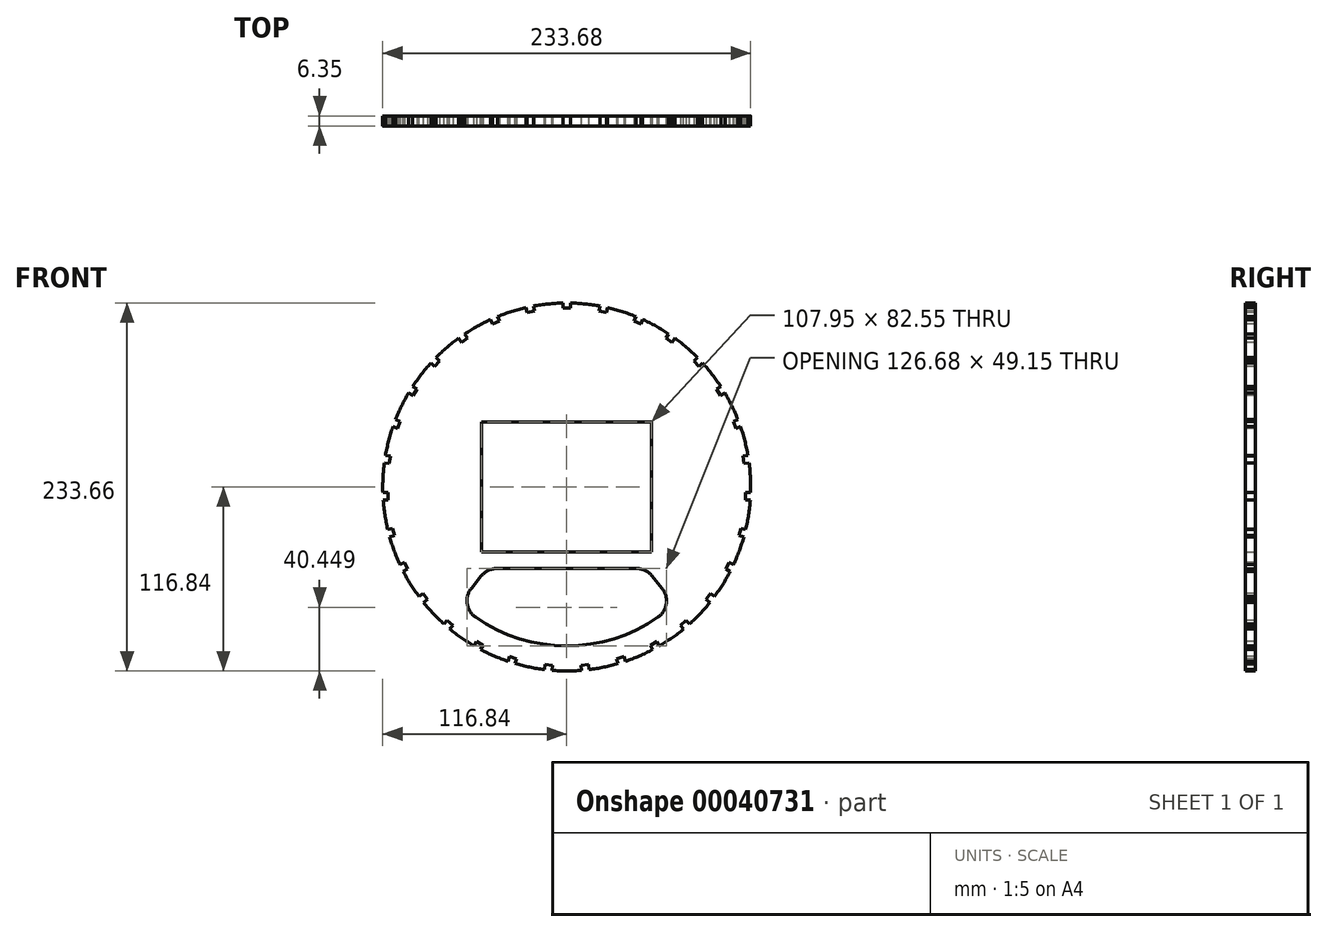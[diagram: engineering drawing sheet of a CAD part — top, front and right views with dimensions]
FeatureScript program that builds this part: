
annotation { "Feature Type Name" : "Feature", "Feature Type Description" : "" }
export const myFeature = defineFeature(function(context is Context, id is Id, definition is map)
    precondition{}
    {
        {
            var Q0;
            Q0=qCreatedBy(makeId("Front.planeOp"),FACE);
            var sketch = newSketch(context, id + "F0", { "sketchPlane" : qUnion([Q0])});
            skCircle(sketch, "E0", {"center": v(0, 0) * mm, "radius": 116.84 * mm});
            skLineSegment(sketch, "E1.bottom", {"start": v(-53.97, 41.28) * mm, "end": v(53.98, 41.28) * mm});
            skLineSegment(sketch, "E1.top", {"start": v(-53.97, -41.27) * mm, "end": v(53.98, -41.27) * mm});
            skLineSegment(sketch, "E1.left", {"start": v(-53.97, 41.28) * mm, "end": v(-53.97, -41.27) * mm});
            skLineSegment(sketch, "E1.right", {"start": v(53.98, 41.28) * mm, "end": v(53.98, -41.27) * mm});
            skLineSegment(sketch, "E2", {"start": v(0, 121.96) * mm, "end": v(0, -123.35) * mm, "construction": true});
            skLineSegment(sketch, "E3", {"start": v(-144.98, 0) * mm, "end": v(150.29, 0) * mm, "construction": true});
            skArc(sketch, "E4", {"start": v(-57.96, -82.67) * mm, "mid": v(0, -100.97) * mm, "end": v(57.96, -82.67) * mm});
            skLineSegment(sketch, "E5", {"start": v(-60.54, -64.28) * mm, "end": v(-54.26, -56.53) * mm});
            skLineSegment(sketch, "E6", {"start": v(-44.38, -51.82) * mm, "end": v(44.38, -51.82) * mm});
            skLineSegment(sketch, "E7", {"start": v(54.26, -56.53) * mm, "end": v(60.54, -64.28) * mm});
            skPoint(sketch, "E8.visualSharp", {"position": v(-50.44, -51.82) * mm});
            skArc(sketch, "E8.filletArc", {"start": v(-44.38, -51.82) * mm, "mid": v(-49.85, -53.05) * mm, "end": v(-54.26, -56.53) * mm});
            skPoint(sketch, "E9.visualSharp", {"position": v(50.44, -51.82) * mm});
            skArc(sketch, "E9.filletArc", {"start": v(54.26, -56.53) * mm, "mid": v(49.85, -53.05) * mm, "end": v(44.38, -51.82) * mm});
            skPoint(sketch, "E10.visualSharp", {"position": v(-68.52, -74.15) * mm});
            skArc(sketch, "E10.filletArc", {"start": v(-60.54, -64.28) * mm, "mid": v(-63.24, -74.04) * mm, "end": v(-57.96, -82.67) * mm});
            skPoint(sketch, "E11.visualSharp", {"position": v(68.52, -74.15) * mm});
            skArc(sketch, "E11.filletArc", {"start": v(57.96, -82.67) * mm, "mid": v(63.24, -74.04) * mm, "end": v(60.54, -64.28) * mm});
            skLineSegment(sketch, "E12.anchor1", {"start": v(0, 0) * mm, "end": v(-68.52, -74.15) * mm, "construction": true});
            skLineSegment(sketch, "E12.anchor2", {"start": v(0, 0) * mm, "end": v(-68.52, -74.15) * mm, "construction": true});
            skSolve(sketch);
        }
        {
            var Q0;
            Q0=makeQuery(id+"F0.imprint","IMPRINT",FACE,{"disambiguationData":[TD([[makeQuery(id+"F0.imprint","IMPRINT",EDGE,{"derivedFrom":sQuery(id+"F0.wireOp",EDGE,"E0")}),1.0]])]});
            extrude(context, id + "F1", {"entities" : qUnion([Q0]), "depth" : 6.35 * mm});
        }
        {
            var Q0;
            Q0=makeQuery(id+"F1.opExtrude","CAP_FACE",FACE,{"disambiguationData":[OSD([sQuery(id+"F0.wireOp",EDGE,"E0"),sQuery(id+"F0.wireOp",EDGE,"E1.bottom"),sQuery(id+"F0.wireOp",EDGE,"E1.top"),sQuery(id+"F0.wireOp",EDGE,"E1.left"),sQuery(id+"F0.wireOp",EDGE,"E1.right"),sQuery(id+"F0.wireOp",EDGE,"E4"),sQuery(id+"F0.wireOp",EDGE,"E5"),sQuery(id+"F0.wireOp",EDGE,"E6"),sQuery(id+"F0.wireOp",EDGE,"E7"),sQuery(id+"F0.wireOp",EDGE,"E8.filletArc"),sQuery(id+"F0.wireOp",EDGE,"E9.filletArc"),sQuery(id+"F0.wireOp",EDGE,"E10.filletArc"),sQuery(id+"F0.wireOp",EDGE,"E11.filletArc")])],"isStart":false});
            var sketch = newSketch(context, id + "F2", { "sketchPlane" : qUnion([Q0])});
            skLineSegment(sketch, "E13", {"start": v(0, 66.33) * mm, "end": v(0, 127.65) * mm, "construction": true});
            skLineSegment(sketch, "E14.bottom", {"start": v(-2.38, 116.84) * mm, "end": v(2.38, 116.84) * mm});
            skLineSegment(sketch, "E14.top", {"start": v(-2.38, 113.66) * mm, "end": v(2.38, 113.66) * mm});
            skLineSegment(sketch, "E14.left", {"start": v(-2.38, 116.84) * mm, "end": v(-2.38, 113.66) * mm});
            skLineSegment(sketch, "E14.right", {"start": v(2.38, 116.84) * mm, "end": v(2.38, 113.66) * mm});
            skLineSegment(sketch, "E15.1.0", {"start": v(21.19, 114.93) * mm, "end": v(25.85, 113.97) * mm});
            skLineSegment(sketch, "E15.1.1", {"start": v(20.55, 111.82) * mm, "end": v(25.21, 110.86) * mm});
            skLineSegment(sketch, "E15.1.2", {"start": v(21.19, 114.93) * mm, "end": v(20.55, 111.82) * mm});
            skLineSegment(sketch, "E15.1.3", {"start": v(25.85, 113.97) * mm, "end": v(25.21, 110.86) * mm});
            skLineSegment(sketch, "E15.2.0", {"start": v(43.89, 108.31) * mm, "end": v(48.26, 106.43) * mm});
            skLineSegment(sketch, "E15.2.1", {"start": v(42.64, 105.4) * mm, "end": v(47.01, 103.51) * mm});
            skLineSegment(sketch, "E15.2.2", {"start": v(43.89, 108.31) * mm, "end": v(42.64, 105.4) * mm});
            skLineSegment(sketch, "E15.2.3", {"start": v(48.26, 106.43) * mm, "end": v(47.01, 103.51) * mm});
            skLineSegment(sketch, "E15.3.0", {"start": v(64.8, 97.26) * mm, "end": v(68.7, 94.54) * mm});
            skLineSegment(sketch, "E15.3.1", {"start": v(62.98, 94.65) * mm, "end": v(66.89, 91.93) * mm});
            skLineSegment(sketch, "E15.3.2", {"start": v(64.8, 97.26) * mm, "end": v(62.98, 94.65) * mm});
            skLineSegment(sketch, "E15.3.3", {"start": v(68.7, 94.54) * mm, "end": v(66.89, 91.93) * mm});
            skLineSegment(sketch, "E15.4.0", {"start": v(83.04, 82.22) * mm, "end": v(86.33, 78.77) * mm});
            skLineSegment(sketch, "E15.4.1", {"start": v(80.74, 80.04) * mm, "end": v(84.02, 76.59) * mm});
            skLineSegment(sketch, "E15.4.2", {"start": v(83.04, 82.22) * mm, "end": v(80.74, 80.04) * mm});
            skLineSegment(sketch, "E15.4.3", {"start": v(86.33, 78.77) * mm, "end": v(84.02, 76.59) * mm});
            skLineSegment(sketch, "E15.5.0", {"start": v(97.9, 63.83) * mm, "end": v(100.42, 59.78) * mm});
            skLineSegment(sketch, "E15.5.1", {"start": v(95.2, 62.15) * mm, "end": v(97.72, 58.1) * mm});
            skLineSegment(sketch, "E15.5.2", {"start": v(97.9, 63.83) * mm, "end": v(95.2, 62.15) * mm});
            skLineSegment(sketch, "E15.5.3", {"start": v(100.42, 59.78) * mm, "end": v(97.72, 58.1) * mm});
            skLineSegment(sketch, "E15.6.0", {"start": v(108.74, 42.81) * mm, "end": v(110.4, 38.35) * mm});
            skLineSegment(sketch, "E15.6.1", {"start": v(105.76, 41.7) * mm, "end": v(107.42, 37.24) * mm});
            skLineSegment(sketch, "E15.6.2", {"start": v(108.74, 42.81) * mm, "end": v(105.76, 41.7) * mm});
            skLineSegment(sketch, "E15.6.3", {"start": v(110.4, 38.35) * mm, "end": v(107.42, 37.24) * mm});
            skLineSegment(sketch, "E15.7.0", {"start": v(115.13, 20.05) * mm, "end": v(115.85, 15.34) * mm});
            skLineSegment(sketch, "E15.7.1", {"start": v(112, 19.57) * mm, "end": v(112.71, 14.86) * mm});
            skLineSegment(sketch, "E15.7.2", {"start": v(115.13, 20.05) * mm, "end": v(112, 19.57) * mm});
            skLineSegment(sketch, "E15.7.3", {"start": v(115.85, 15.34) * mm, "end": v(112.71, 14.86) * mm});
            skLineSegment(sketch, "E15.8.0", {"start": v(116.81, -3.54) * mm, "end": v(116.57, -8.3) * mm});
            skLineSegment(sketch, "E15.8.1", {"start": v(113.64, -3.38) * mm, "end": v(113.4, -8.13) * mm});
            skLineSegment(sketch, "E15.8.2", {"start": v(116.81, -3.54) * mm, "end": v(113.64, -3.38) * mm});
            skLineSegment(sketch, "E15.8.3", {"start": v(116.57, -8.3) * mm, "end": v(113.4, -8.13) * mm});
            skLineSegment(sketch, "E15.9.0", {"start": v(113.7, -26.98) * mm, "end": v(112.51, -31.6) * mm});
            skLineSegment(sketch, "E15.9.1", {"start": v(110.63, -26.18) * mm, "end": v(109.44, -30.8) * mm});
            skLineSegment(sketch, "E15.9.2", {"start": v(113.7, -26.98) * mm, "end": v(110.63, -26.18) * mm});
            skLineSegment(sketch, "E15.9.3", {"start": v(112.51, -31.6) * mm, "end": v(109.44, -30.8) * mm});
            skLineSegment(sketch, "E15.10.0", {"start": v(105.95, -49.32) * mm, "end": v(103.85, -53.6) * mm});
            skLineSegment(sketch, "E15.10.1", {"start": v(103.1, -47.92) * mm, "end": v(101, -52.2) * mm});
            skLineSegment(sketch, "E15.10.2", {"start": v(105.95, -49.32) * mm, "end": v(103.1, -47.92) * mm});
            skLineSegment(sketch, "E15.10.3", {"start": v(103.85, -53.6) * mm, "end": v(101, -52.2) * mm});
            skLineSegment(sketch, "E15.11.0", {"start": v(93.85, -69.63) * mm, "end": v(90.94, -73.4) * mm});
            skLineSegment(sketch, "E15.11.1", {"start": v(91.34, -67.7) * mm, "end": v(88.43, -71.46) * mm});
            skLineSegment(sketch, "E15.11.2", {"start": v(93.85, -69.63) * mm, "end": v(91.34, -67.7) * mm});
            skLineSegment(sketch, "E15.11.3", {"start": v(90.94, -73.4) * mm, "end": v(88.43, -71.46) * mm});
            skLineSegment(sketch, "E15.12.0", {"start": v(77.91, -87.1) * mm, "end": v(74.3, -90.2) * mm});
            skLineSegment(sketch, "E15.12.1", {"start": v(75.85, -84.7) * mm, "end": v(72.23, -87.8) * mm});
            skLineSegment(sketch, "E15.12.2", {"start": v(77.91, -87.1) * mm, "end": v(75.85, -84.7) * mm});
            skLineSegment(sketch, "E15.12.3", {"start": v(74.3, -90.2) * mm, "end": v(72.23, -87.8) * mm});
            skLineSegment(sketch, "E15.13.0", {"start": v(58.79, -101) * mm, "end": v(54.62, -103.31) * mm});
            skLineSegment(sketch, "E15.13.1", {"start": v(57.24, -98.23) * mm, "end": v(53.08, -100.54) * mm});
            skLineSegment(sketch, "E15.13.2", {"start": v(58.79, -101) * mm, "end": v(57.24, -98.23) * mm});
            skLineSegment(sketch, "E15.13.3", {"start": v(54.62, -103.31) * mm, "end": v(53.08, -100.54) * mm});
            skLineSegment(sketch, "E15.14.0", {"start": v(37.25, -110.77) * mm, "end": v(32.7, -112.2) * mm});
            skLineSegment(sketch, "E15.14.1", {"start": v(36.3, -107.74) * mm, "end": v(31.76, -109.16) * mm});
            skLineSegment(sketch, "E15.14.2", {"start": v(37.25, -110.77) * mm, "end": v(36.3, -107.74) * mm});
            skLineSegment(sketch, "E15.14.3", {"start": v(32.7, -112.2) * mm, "end": v(31.76, -109.16) * mm});
            skLineSegment(sketch, "E15.15.0", {"start": v(14.2, -116) * mm, "end": v(9.45, -116.48) * mm});
            skLineSegment(sketch, "E15.15.1", {"start": v(13.87, -112.84) * mm, "end": v(9.13, -113.32) * mm});
            skLineSegment(sketch, "E15.15.2", {"start": v(14.2, -116) * mm, "end": v(13.87, -112.84) * mm});
            skLineSegment(sketch, "E15.15.3", {"start": v(9.45, -116.48) * mm, "end": v(9.13, -113.32) * mm});
            skLineSegment(sketch, "E15.16.0", {"start": v(-9.45, -116.48) * mm, "end": v(-14.19, -116) * mm});
            skLineSegment(sketch, "E15.16.1", {"start": v(-9.13, -113.32) * mm, "end": v(-13.87, -112.84) * mm});
            skLineSegment(sketch, "E15.16.2", {"start": v(-9.45, -116.48) * mm, "end": v(-9.13, -113.32) * mm});
            skLineSegment(sketch, "E15.16.3", {"start": v(-14.19, -116) * mm, "end": v(-13.87, -112.84) * mm});
            skLineSegment(sketch, "E15.17.0", {"start": v(-32.7, -112.2) * mm, "end": v(-37.25, -110.77) * mm});
            skLineSegment(sketch, "E15.17.1", {"start": v(-31.75, -109.17) * mm, "end": v(-36.3, -107.74) * mm});
            skLineSegment(sketch, "E15.17.2", {"start": v(-32.7, -112.2) * mm, "end": v(-31.75, -109.17) * mm});
            skLineSegment(sketch, "E15.17.3", {"start": v(-37.25, -110.77) * mm, "end": v(-36.3, -107.74) * mm});
            skLineSegment(sketch, "E15.18.0", {"start": v(-54.62, -103.31) * mm, "end": v(-58.78, -101) * mm});
            skLineSegment(sketch, "E15.18.1", {"start": v(-53.08, -100.54) * mm, "end": v(-57.24, -98.23) * mm});
            skLineSegment(sketch, "E15.18.2", {"start": v(-54.62, -103.31) * mm, "end": v(-53.08, -100.54) * mm});
            skLineSegment(sketch, "E15.18.3", {"start": v(-58.78, -101) * mm, "end": v(-57.24, -98.23) * mm});
            skLineSegment(sketch, "E15.19.0", {"start": v(-74.3, -90.2) * mm, "end": v(-77.91, -87.1) * mm});
            skLineSegment(sketch, "E15.19.1", {"start": v(-72.23, -87.8) * mm, "end": v(-75.84, -84.7) * mm});
            skLineSegment(sketch, "E15.19.2", {"start": v(-74.3, -90.2) * mm, "end": v(-72.23, -87.8) * mm});
            skLineSegment(sketch, "E15.19.3", {"start": v(-77.91, -87.1) * mm, "end": v(-75.84, -84.7) * mm});
            skLineSegment(sketch, "E15.20.0", {"start": v(-90.94, -73.4) * mm, "end": v(-93.85, -69.64) * mm});
            skLineSegment(sketch, "E15.20.1", {"start": v(-88.43, -71.46) * mm, "end": v(-91.34, -67.7) * mm});
            skLineSegment(sketch, "E15.20.2", {"start": v(-90.94, -73.4) * mm, "end": v(-88.43, -71.46) * mm});
            skLineSegment(sketch, "E15.20.3", {"start": v(-93.85, -69.64) * mm, "end": v(-91.34, -67.7) * mm});
            skLineSegment(sketch, "E15.21.0", {"start": v(-103.85, -53.6) * mm, "end": v(-105.95, -49.32) * mm});
            skLineSegment(sketch, "E15.21.1", {"start": v(-101, -52.2) * mm, "end": v(-103.1, -47.92) * mm});
            skLineSegment(sketch, "E15.21.2", {"start": v(-103.85, -53.6) * mm, "end": v(-101, -52.2) * mm});
            skLineSegment(sketch, "E15.21.3", {"start": v(-105.95, -49.32) * mm, "end": v(-103.1, -47.92) * mm});
            skLineSegment(sketch, "E15.22.0", {"start": v(-112.51, -31.6) * mm, "end": v(-113.7, -26.98) * mm});
            skLineSegment(sketch, "E15.22.1", {"start": v(-109.44, -30.8) * mm, "end": v(-110.63, -26.19) * mm});
            skLineSegment(sketch, "E15.22.2", {"start": v(-112.51, -31.6) * mm, "end": v(-109.44, -30.8) * mm});
            skLineSegment(sketch, "E15.22.3", {"start": v(-113.7, -26.98) * mm, "end": v(-110.63, -26.19) * mm});
            skLineSegment(sketch, "E15.23.0", {"start": v(-116.57, -8.3) * mm, "end": v(-116.81, -3.54) * mm});
            skLineSegment(sketch, "E15.23.1", {"start": v(-113.4, -8.14) * mm, "end": v(-113.64, -3.38) * mm});
            skLineSegment(sketch, "E15.23.2", {"start": v(-116.57, -8.3) * mm, "end": v(-113.4, -8.14) * mm});
            skLineSegment(sketch, "E15.23.3", {"start": v(-116.81, -3.54) * mm, "end": v(-113.64, -3.38) * mm});
            skLineSegment(sketch, "E15.24.0", {"start": v(-115.85, 15.34) * mm, "end": v(-115.13, 20.05) * mm});
            skLineSegment(sketch, "E15.24.1", {"start": v(-112.72, 14.86) * mm, "end": v(-112, 19.56) * mm});
            skLineSegment(sketch, "E15.24.2", {"start": v(-115.85, 15.34) * mm, "end": v(-112.72, 14.86) * mm});
            skLineSegment(sketch, "E15.24.3", {"start": v(-115.13, 20.05) * mm, "end": v(-112, 19.56) * mm});
            skLineSegment(sketch, "E15.25.0", {"start": v(-110.4, 38.34) * mm, "end": v(-108.74, 42.81) * mm});
            skLineSegment(sketch, "E15.25.1", {"start": v(-107.42, 37.24) * mm, "end": v(-105.76, 41.7) * mm});
            skLineSegment(sketch, "E15.25.2", {"start": v(-110.4, 38.34) * mm, "end": v(-107.42, 37.24) * mm});
            skLineSegment(sketch, "E15.25.3", {"start": v(-108.74, 42.81) * mm, "end": v(-105.76, 41.7) * mm});
            skLineSegment(sketch, "E15.26.0", {"start": v(-100.42, 59.78) * mm, "end": v(-97.9, 63.82) * mm});
            skLineSegment(sketch, "E15.26.1", {"start": v(-97.72, 58.1) * mm, "end": v(-95.2, 62.14) * mm});
            skLineSegment(sketch, "E15.26.2", {"start": v(-100.42, 59.78) * mm, "end": v(-97.72, 58.1) * mm});
            skLineSegment(sketch, "E15.26.3", {"start": v(-97.9, 63.82) * mm, "end": v(-95.2, 62.14) * mm});
            skLineSegment(sketch, "E15.27.0", {"start": v(-86.33, 78.77) * mm, "end": v(-83.05, 82.22) * mm});
            skLineSegment(sketch, "E15.27.1", {"start": v(-84.03, 76.58) * mm, "end": v(-80.74, 80.04) * mm});
            skLineSegment(sketch, "E15.27.2", {"start": v(-86.33, 78.77) * mm, "end": v(-84.03, 76.58) * mm});
            skLineSegment(sketch, "E15.27.3", {"start": v(-83.05, 82.22) * mm, "end": v(-80.74, 80.04) * mm});
            skLineSegment(sketch, "E15.28.0", {"start": v(-68.7, 94.54) * mm, "end": v(-64.8, 97.26) * mm});
            skLineSegment(sketch, "E15.28.1", {"start": v(-66.89, 91.93) * mm, "end": v(-62.98, 94.65) * mm});
            skLineSegment(sketch, "E15.28.2", {"start": v(-68.7, 94.54) * mm, "end": v(-66.89, 91.93) * mm});
            skLineSegment(sketch, "E15.28.3", {"start": v(-64.8, 97.26) * mm, "end": v(-62.98, 94.65) * mm});
            skLineSegment(sketch, "E15.29.0", {"start": v(-48.27, 106.43) * mm, "end": v(-43.9, 108.3) * mm});
            skLineSegment(sketch, "E15.29.1", {"start": v(-47.01, 103.51) * mm, "end": v(-42.64, 105.4) * mm});
            skLineSegment(sketch, "E15.29.2", {"start": v(-48.27, 106.43) * mm, "end": v(-47.01, 103.51) * mm});
            skLineSegment(sketch, "E15.29.3", {"start": v(-43.9, 108.3) * mm, "end": v(-42.64, 105.4) * mm});
            skLineSegment(sketch, "E15.30.0", {"start": v(-25.85, 113.97) * mm, "end": v(-21.19, 114.93) * mm});
            skLineSegment(sketch, "E15.30.1", {"start": v(-25.21, 110.86) * mm, "end": v(-20.55, 111.82) * mm});
            skLineSegment(sketch, "E15.30.2", {"start": v(-25.85, 113.97) * mm, "end": v(-25.21, 110.86) * mm});
            skLineSegment(sketch, "E15.30.3", {"start": v(-21.19, 114.93) * mm, "end": v(-20.55, 111.82) * mm});
            skLineSegment(sketch, "E15.31.1", {"start": v(-2.38, 113.66) * mm, "end": v(2.38, 113.67) * mm});
            skLineSegment(sketch, "E15.31.3", {"start": v(2.38, 116.84) * mm, "end": v(2.38, 113.67) * mm});
            skPoint(sketch, "E15.center", {"position": v(0, 0) * mm});
            skLineSegment(sketch, "E15.anchor1", {"start": v(0, 0) * mm, "end": v(-2.38, 116.84) * mm, "construction": true});
            skLineSegment(sketch, "E15.anchor2", {"start": v(0, 0) * mm, "end": v(-2.38, 116.84) * mm, "construction": true});
            skSolve(sketch);
        }
        {
            var Q0;
            Q0 = qSketchRegion(id + "F2", true);
            extrude(context, id + "F3", {"entities" : qUnion([Q0]), "operationType" : NewBodyOperationType.REMOVE, "endBound" : BoundingType.SYMMETRIC, "oppositeDirection" : true, "depth" : 25.4 * mm});
        }
        {
            var Q0;
            Q0=makeQuery(id+"F1.opExtrude","SWEPT_BODY",BODY,{"disambiguationData":[OSD([sQuery(id+"F0.wireOp",EDGE,"E0"),sQuery(id+"F0.wireOp",EDGE,"E1.bottom"),sQuery(id+"F0.wireOp",EDGE,"E1.top"),sQuery(id+"F0.wireOp",EDGE,"E1.left"),sQuery(id+"F0.wireOp",EDGE,"E1.right"),sQuery(id+"F0.wireOp",EDGE,"E4"),sQuery(id+"F0.wireOp",EDGE,"E5"),sQuery(id+"F0.wireOp",EDGE,"E6"),sQuery(id+"F0.wireOp",EDGE,"E7"),sQuery(id+"F0.wireOp",EDGE,"E8.filletArc"),sQuery(id+"F0.wireOp",EDGE,"E9.filletArc"),sQuery(id+"F0.wireOp",EDGE,"E10.filletArc"),sQuery(id+"F0.wireOp",EDGE,"E11.filletArc")])]});
            transform(context, id + "F4", {"entities" : qUnion([Q0]), "transformType" : TransformType.TRANSLATION_3D, "dx" : 0 * mm, "dy" : 87.31 * mm, "dz" : 0 * mm, "makeCopy" : true});
        }
        {
            var Q0;
            Q0=makeQuery(id+"F4.opPattern","COPY",BODY,{"derivedFrom":makeQuery(id+"F1.opExtrude","SWEPT_BODY",BODY,{"disambiguationData":[OSD([sQuery(id+"F0.wireOp",EDGE,"E0"),sQuery(id+"F0.wireOp",EDGE,"E1.bottom"),sQuery(id+"F0.wireOp",EDGE,"E1.top"),sQuery(id+"F0.wireOp",EDGE,"E1.left"),sQuery(id+"F0.wireOp",EDGE,"E1.right"),sQuery(id+"F0.wireOp",EDGE,"E4"),sQuery(id+"F0.wireOp",EDGE,"E5"),sQuery(id+"F0.wireOp",EDGE,"E6"),sQuery(id+"F0.wireOp",EDGE,"E7"),sQuery(id+"F0.wireOp",EDGE,"E8.filletArc"),sQuery(id+"F0.wireOp",EDGE,"E9.filletArc"),sQuery(id+"F0.wireOp",EDGE,"E10.filletArc"),sQuery(id+"F0.wireOp",EDGE,"E11.filletArc")])]}),"instanceName":"1"});
            deleteBodies(context, id + "F5", {"entities" : qUnion([Q0])});
        }
    });
